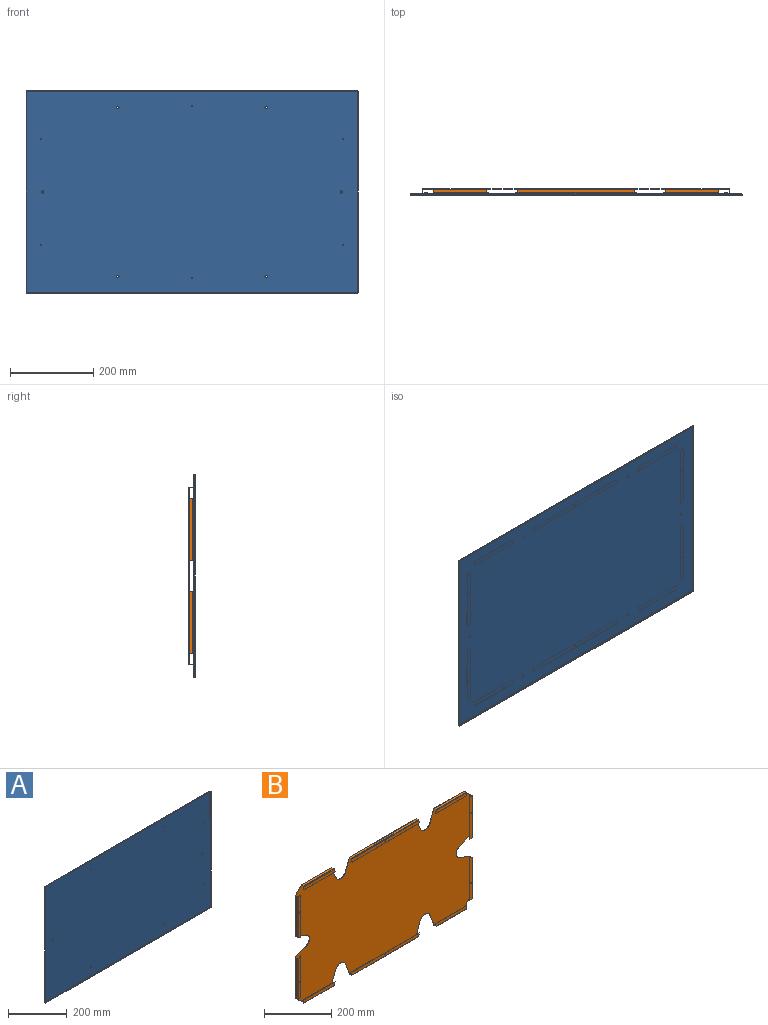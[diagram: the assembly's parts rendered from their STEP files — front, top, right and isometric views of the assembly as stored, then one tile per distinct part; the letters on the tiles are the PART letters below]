
ASSEMBLY  parts=2 mates=1
PART A: 50 faces, bbox 796.6x4x485.5 mm
  f0: plane 793.1x0.86mm, normal (0,-1,0), area 684.9mm2, adj f1,f2,f3,f4
  f1: plane 2.31x0.86mm, normal (1,0,0), area 2mm2, adj f0,f3,f4,f47
  f2: plane 2.31x0.86mm, normal (-1,0,0), area 2mm2, adj f0,f3,f4,f46
  f3: plane 793.1x2.31mm, normal (0,0,1), area 1833.2mm2, adj f0,f1,f2,f48
  f4: plane 793.1x2.31mm, normal (0,0,-1), area 1833.2mm2, adj f0,f1,f2,f49
  f5: cylinder r=1.63mm len=3.26mm, axis (0,-1,0), area 8.9mm2, adj f17,f18
  f6: cylinder r=1.63mm len=3.26mm, axis (0,-1,0), area 8.9mm2, adj f17,f18
  f7: cylinder r=1.63mm len=3.26mm, axis (0,-1,0), area 8.9mm2, adj f17,f18
  f8: cylinder r=1.63mm len=3.26mm, axis (0,-1,0), area 8.9mm2, adj f17,f18
  f9: cylinder r=1.63mm len=3.26mm, axis (0,-1,0), area 8.9mm2, adj f17,f18
  f10: cylinder r=1.63mm len=3.26mm, axis (0,-1,0), area 8.9mm2, adj f17,f18
  f11: cylinder r=2.77mm len=5.54mm, axis (0,-1,0), area 15mm2, adj f17,f18
  f12: cylinder r=2.77mm len=5.54mm, axis (0,-1,0), area 15mm2, adj f17,f18
  f13: cylinder r=2.77mm len=5.54mm, axis (0,-1,0), area 15mm2, adj f17,f18
  f14: cylinder r=2.77mm len=5.54mm, axis (0,-1,0), area 15mm2, adj f17,f18
  f15: cylinder r=2.77mm len=5.54mm, axis (0,-1,0), area 15mm2, adj f17,f18
  f16: cylinder r=2.77mm len=5.54mm, axis (0,-1,0), area 15mm2, adj f17,f18
  f17: plane 793.1x482.04mm, normal (0,1,0), area 382113.3mm2, adj f5,f6,f7,f8,f9,f10,f11,f12
  f18: plane 793.1x482.04mm, normal (0,-1,0), area 382113.3mm2, adj f5,f6,f7,f8,f9,f10,f11,f12
  f19: plane 793.1x0.86mm, normal (0,-1,0), area 684.9mm2, adj f20,f21,f22,f23
  f20: plane 2.31x0.86mm, normal (-1,0,0), area 2mm2, adj f19,f22,f23,f24
  f21: plane 2.31x0.86mm, normal (1,0,0), area 2mm2, adj f19,f22,f23,f25
  f22: plane 793.1x2.31mm, normal (0,0,-1), area 1833.2mm2, adj f19,f20,f21,f26
  f23: plane 793.1x2.31mm, normal (0,0,1), area 1833.2mm2, adj f19,f20,f21,f27
  f24: plane 1.73x1.73mm, normal (-1,0,0), area 1.8mm2, adj f20,f26,f27,f42
  f25: plane 1.73x1.73mm, normal (1,0,0), area 1.8mm2, adj f21,f26,f27,f33
  f26: cylinder r=1.73mm len=793.1mm, axis (-1,0,0), area 2151.7mm2, adj f17,f22,f24,f25
  f27: cylinder r=0.86mm len=793.1mm, axis (-1,0,0), area 1075.9mm2, adj f18,f23,f24,f25
  f28: plane 482.04x0.86mm, normal (0,-1,0), area 416.3mm2, adj f29,f30,f31,f32
  f29: plane 2.31x0.86mm, normal (0,0,-1), area 2mm2, adj f28,f31,f32,f33
  f30: plane 2.31x0.86mm, normal (0,0,1), area 2mm2, adj f28,f31,f32,f34
  f31: plane 482.04x2.31mm, normal (1,0,0), area 1114.2mm2, adj f28,f29,f30,f35
  f32: plane 482.04x2.31mm, normal (-1,0,0), area 1114.2mm2, adj f28,f29,f30,f36
  f33: plane 1.73x1.73mm, normal (0,0,-1), area 1.8mm2, adj f25,f29,f35,f36
  f34: plane 1.73x1.73mm, normal (0,0,1), area 1.8mm2, adj f30,f35,f36,f47
  f35: cylinder r=1.73mm len=482.04mm, axis (0,0,-1), area 1307.8mm2, adj f17,f31,f33,f34
  f36: cylinder r=0.86mm len=482.04mm, axis (0,0,-1), area 653.9mm2, adj f18,f32,f33,f34
  f37: plane 482.04x0.86mm, normal (0,-1,0), area 416.3mm2, adj f38,f39,f40,f41
  f38: plane 2.31x0.86mm, normal (0,0,1), area 2mm2, adj f37,f40,f41,f43
  f39: plane 2.31x0.86mm, normal (0,0,-1), area 2mm2, adj f37,f40,f41,f42
  f40: plane 482.04x2.31mm, normal (-1,0,0), area 1114.2mm2, adj f37,f38,f39,f44
  f41: plane 482.04x2.31mm, normal (1,0,0), area 1114.2mm2, adj f37,f38,f39,f45
  f42: plane 1.73x1.73mm, normal (0,0,-1), area 1.8mm2, adj f24,f39,f44,f45
  f43: plane 1.73x1.73mm, normal (0,0,1), area 1.8mm2, adj f38,f44,f45,f46
  f44: cylinder r=1.73mm len=482.04mm, axis (0,0,-1), area 1307.8mm2, adj f17,f40,f42,f43
  f45: cylinder r=0.86mm len=482.04mm, axis (0,0,-1), area 653.9mm2, adj f18,f41,f42,f43
  f46: plane 1.73x1.73mm, normal (-1,0,0), area 1.8mm2, adj f2,f43,f48,f49
  f47: plane 1.73x1.73mm, normal (1,0,0), area 1.8mm2, adj f1,f34,f48,f49
  f48: cylinder r=1.73mm len=793.1mm, axis (-1,0,0), area 2151.7mm2, adj f3,f17,f46,f47
  f49: cylinder r=0.86mm len=793.1mm, axis (-1,0,0), area 1075.9mm2, adj f4,f18,f46,f47
PART B: 200 faces, bbox 737.7x11.1x426.6 mm
  f0: plane 43.46x16.69mm, normal (-0.36,0,0.93), area 40.2mm2, adj f1,f22,f23,f143
  f1: cylinder r=22.23mm len=41.5mm, axis (0,-1,0), area 46.2mm2, adj f0,f2,f22,f23
  f2: plane 43.46x16.69mm, normal (-0.36,0,-0.93), area 40.2mm2, adj f1,f22,f23,f196
  f3: plane 23.67x23.67mm, normal (-0.71,0,0.71), area 28.9mm2, adj f22,f23,f111,f197
  f4: plane 43.46x16.69mm, normal (0.93,0,0.36), area 40.2mm2, adj f5,f22,f23,f112
  f5: cylinder r=22.23mm len=41.5mm, axis (0,-1,0), area 46.2mm2, adj f4,f6,f22,f23
  f6: plane 43.46x16.69mm, normal (-0.93,0,0.36), area 40.2mm2, adj f5,f22,f23,f107
  f7: plane 43.46x16.69mm, normal (0.93,0,0.36), area 40.2mm2, adj f8,f22,f23,f108
  f8: cylinder r=22.23mm len=41.5mm, axis (0,-1,0), area 46.2mm2, adj f7,f9,f22,f23
  f9: plane 43.46x16.69mm, normal (-0.93,0,0.36), area 40.2mm2, adj f8,f22,f23,f89
  f10: plane 23.67x23.67mm, normal (0.71,0,0.71), area 28.9mm2, adj f22,f23,f90,f179
  f11: plane 43.46x16.69mm, normal (0.36,0,-0.93), area 40.2mm2, adj f12,f22,f23,f178
  f12: cylinder r=22.23mm len=41.5mm, axis (0,-1,0), area 46.2mm2, adj f11,f13,f22,f23
  f13: plane 43.46x16.69mm, normal (0.36,0,0.93), area 40.2mm2, adj f12,f22,f23,f161
  f14: plane 23.67x23.67mm, normal (0.71,0,-0.71), area 28.9mm2, adj f22,f23,f73,f160
  f15: plane 43.46x16.69mm, normal (-0.93,0,-0.36), area 40.2mm2, adj f16,f22,f23,f72
  f16: cylinder r=22.23mm len=41.5mm, axis (0,-1,0), area 46.2mm2, adj f15,f17,f22,f23
  f17: plane 43.46x16.69mm, normal (0.93,0,-0.36), area 40.2mm2, adj f16,f22,f23,f56
  f18: plane 43.46x16.69mm, normal (-0.93,0,-0.36), area 40.2mm2, adj f19,f22,f23,f55
  f19: cylinder r=22.23mm len=41.5mm, axis (0,-1,0), area 46.2mm2, adj f18,f20,f22,f23
  f20: plane 43.46x16.69mm, normal (0.93,0,-0.36), area 40.2mm2, adj f19,f22,f23,f38
  f21: plane 23.67x23.67mm, normal (-0.71,0,-0.71), area 28.9mm2, adj f22,f23,f37,f142
  f22: plane 734.23x423.16mm, normal (0,1,0), area 291828.6mm2, adj f0,f1,f2,f3,f4,f5,f6,f7
  f23: plane 734.23x423.16mm, normal (0,-1,0), area 291828.6mm2, adj f0,f1,f2,f3,f4,f5,f6,f7
  f24: plane 10.97x4.21mm, normal (0.93,0,-0.36), area 10.2mm2, adj f25,f27,f28,f30
  f25: plane 131.55x0.86mm, normal (0,0,1), area 113.6mm2, adj f24,f26,f27,f28
  f26: plane 10.97x0.86mm, normal (-1,0,0), area 9.5mm2, adj f25,f27,f28,f29
  f27: plane 131.55x10.97mm, normal (0,-1,0), area 1420.4mm2, adj f24,f25,f26,f31
  f28: plane 131.55x10.97mm, normal (0,1,0), area 1420.4mm2, adj f24,f25,f26,f32
  f29: plane 1.73x1.73mm, normal (-1,0,0), area 1.8mm2, adj f26,f31,f32,f33
  f30: bspline ~1.73x1.73mm, area 1.8mm2, adj f24,f31,f32,f34
  f31: cylinder r=1.73mm len=127.34mm, axis (-1,0,0), area 345.5mm2, adj f27,f29,f30,f35
  f32: cylinder r=0.86mm len=127.34mm, axis (-1,0,0), area 172.7mm2, adj f28,f29,f30,f36
  f33: plane 7.66x0.86mm, normal (-1,0,0), area 6.6mm2, adj f29,f35,f36,f37
  f34: plane 7.66x0.86mm, normal (1,0,0), area 6.6mm2, adj f30,f35,f36,f38
  f35: plane 127.32x7.66mm, normal (0,0,-1), area 975mm2, adj f31,f33,f34,f39
  f36: plane 127.32x7.66mm, normal (0,0,1), area 975mm2, adj f32,f33,f34,f40
  f37: bspline ~1.73x1.73mm, area 2mm2, adj f21,f33,f39,f40
  f38: bspline ~1.73x1.73mm, area 1.8mm2, adj f20,f34,f39,f40
  f39: cylinder r=1.73mm len=128.2mm, axis (-1,0,0), area 346.1mm2, adj f22,f35,f37,f38
  f40: cylinder r=0.86mm len=128.2mm, axis (-1,0,0), area 173mm2, adj f23,f36,f37,f38
  f41: plane 10.97x4.21mm, normal (0.93,0,-0.36), area 10.2mm2, adj f42,f45,f46,f48
  f42: plane 289.15x0.86mm, normal (0,0,1), area 249.7mm2, adj f41,f43,f45,f46
  f43: plane 10.97x4.21mm, normal (-0.93,0,-0.36), area 10.2mm2, adj f42,f45,f46,f47
  f44: cylinder r=1.63mm len=3.26mm, axis (0,-1,0), area 8.9mm2, adj f45,f46
  f45: plane 289.15x10.97mm, normal (0,-1,0), area 3118.2mm2, adj f41,f42,f43,f44,f49
  f46: plane 289.15x10.97mm, normal (0,1,0), area 3118.2mm2, adj f41,f42,f43,f44,f50
  f47: bspline ~1.73x1.73mm, area 1.8mm2, adj f43,f49,f50,f51
  f48: bspline ~1.73x1.73mm, area 1.8mm2, adj f41,f49,f50,f52
  f49: cylinder r=1.73mm len=280.73mm, axis (-1,0,0), area 761.6mm2, adj f45,f47,f48,f53
  f50: cylinder r=0.86mm len=280.73mm, axis (-1,0,0), area 380.8mm2, adj f46,f47,f48,f54
  f51: plane 7.66x0.86mm, normal (-1,0,0), area 6.6mm2, adj f47,f53,f54,f55
  f52: plane 7.66x0.86mm, normal (1,0,0), area 6.6mm2, adj f48,f53,f54,f56
  f53: plane 280.69x7.66mm, normal (0,0,-1), area 2149.6mm2, adj f49,f51,f52,f57
  f54: plane 280.69x7.66mm, normal (0,0,1), area 2149.6mm2, adj f50,f51,f52,f58
  f55: bspline ~1.73x1.73mm, area 1.8mm2, adj f18,f51,f57,f58
  f56: bspline ~1.73x1.73mm, area 1.8mm2, adj f17,f52,f57,f58
  f57: cylinder r=1.73mm len=280.73mm, axis (-1,0,0), area 761.6mm2, adj f22,f53,f55,f56
  f58: cylinder r=0.86mm len=280.73mm, axis (-1,0,0), area 380.8mm2, adj f23,f54,f55,f56
  f59: plane 10.97x0.86mm, normal (1,0,0), area 9.5mm2, adj f60,f62,f63,f65
  f60: plane 131.55x0.86mm, normal (0,0,1), area 113.6mm2, adj f59,f61,f62,f63
  f61: plane 10.97x4.21mm, normal (-0.93,0,-0.36), area 10.2mm2, adj f60,f62,f63,f64
  f62: plane 131.55x10.97mm, normal (0,-1,0), area 1420.4mm2, adj f59,f60,f61,f66
  f63: plane 131.55x10.97mm, normal (0,1,0), area 1420.4mm2, adj f59,f60,f61,f67
  f64: bspline ~1.73x1.73mm, area 1.8mm2, adj f61,f66,f67,f69
  f65: plane 1.73x1.73mm, normal (1,0,0), area 1.8mm2, adj f59,f66,f67,f68
  f66: cylinder r=1.73mm len=127.34mm, axis (-1,0,0), area 345.5mm2, adj f62,f64,f65,f70
  f67: cylinder r=0.86mm len=127.34mm, axis (-1,0,0), area 172.7mm2, adj f63,f64,f65,f71
  f68: plane 7.66x0.86mm, normal (1,0,0), area 6.6mm2, adj f65,f70,f71,f73
  f69: plane 7.66x0.86mm, normal (-1,0,0), area 6.6mm2, adj f64,f70,f71,f72
  f70: plane 127.32x7.66mm, normal (0,0,-1), area 975mm2, adj f66,f68,f69,f74
  f71: plane 127.32x7.66mm, normal (0,0,1), area 975mm2, adj f67,f68,f69,f75
  f72: bspline ~1.73x1.73mm, area 1.8mm2, adj f15,f69,f74,f75
  f73: bspline ~1.73x1.73mm, area 2mm2, adj f14,f68,f74,f75
  f74: cylinder r=1.73mm len=128.2mm, axis (-1,0,0), area 346.1mm2, adj f22,f70,f72,f73
  f75: cylinder r=0.86mm len=128.2mm, axis (-1,0,0), area 173mm2, adj f23,f71,f72,f73
  f76: plane 7.66x0.86mm, normal (1,0,0), area 6.6mm2, adj f78,f79,f81,f90
  f77: plane 7.66x0.86mm, normal (-1,0,0), area 6.6mm2, adj f78,f79,f80,f89
  f78: plane 127.32x7.66mm, normal (0,0,1), area 975mm2, adj f76,f77,f82,f91
  f79: plane 127.32x7.66mm, normal (0,0,-1), area 975mm2, adj f76,f77,f83,f92
  f80: bspline ~1.73x1.73mm, area 1.8mm2, adj f77,f82,f83,f84
  f81: plane 1.73x1.73mm, normal (1,0,0), area 1.8mm2, adj f76,f82,f83,f86
  f82: cylinder r=1.73mm len=127.34mm, axis (-1,0,0), area 345.5mm2, adj f78,f80,f81,f87
  f83: cylinder r=0.86mm len=127.34mm, axis (-1,0,0), area 172.7mm2, adj f79,f80,f81,f88
  f84: plane 10.97x4.21mm, normal (-0.93,0,0.36), area 10.2mm2, adj f80,f85,f87,f88
  f85: plane 131.55x0.86mm, normal (0,0,-1), area 113.6mm2, adj f84,f86,f87,f88
  f86: plane 10.97x0.86mm, normal (1,0,0), area 9.5mm2, adj f81,f85,f87,f88
  f87: plane 131.55x10.97mm, normal (0,-1,0), area 1420.4mm2, adj f82,f84,f85,f86
  f88: plane 131.55x10.97mm, normal (0,1,0), area 1420.4mm2, adj f83,f84,f85,f86
  f89: bspline ~1.73x1.73mm, area 1.8mm2, adj f9,f77,f91,f92
  f90: bspline ~1.73x1.73mm, area 2mm2, adj f10,f76,f91,f92
  f91: cylinder r=1.73mm len=128.2mm, axis (-1,0,0), area 346.1mm2, adj f22,f78,f89,f90
  f92: cylinder r=0.86mm len=128.2mm, axis (-1,0,0), area 173mm2, adj f23,f79,f89,f90
  f93: plane 10.97x4.21mm, normal (-0.93,0,0.36), area 10.2mm2, adj f94,f97,f98,f99
  f94: plane 289.15x0.86mm, normal (0,0,-1), area 249.7mm2, adj f93,f95,f97,f98
  f95: plane 10.97x4.21mm, normal (0.93,0,0.36), area 10.2mm2, adj f94,f97,f98,f100
  f96: cylinder r=1.63mm len=3.26mm, axis (0,-1,0), area 8.9mm2, adj f97,f98
  f97: plane 289.15x10.97mm, normal (0,-1,0), area 3118.2mm2, adj f93,f94,f95,f96,f101
  f98: plane 289.15x10.97mm, normal (0,1,0), area 3118.2mm2, adj f93,f94,f95,f96,f102
  f99: bspline ~1.73x1.73mm, area 1.8mm2, adj f93,f101,f102,f103
  f100: bspline ~1.73x1.73mm, area 1.8mm2, adj f95,f101,f102,f104
  f101: cylinder r=1.73mm len=280.73mm, axis (-1,0,0), area 761.6mm2, adj f97,f99,f100,f105
  f102: cylinder r=0.86mm len=280.73mm, axis (-1,0,0), area 380.8mm2, adj f98,f99,f100,f106
  f103: plane 7.66x0.86mm, normal (-1,0,0), area 6.6mm2, adj f99,f105,f106,f107
  f104: plane 7.66x0.86mm, normal (1,0,0), area 6.6mm2, adj f100,f105,f106,f108
  f105: plane 280.69x7.66mm, normal (0,0,1), area 2149.6mm2, adj f101,f103,f104,f109
  f106: plane 280.69x7.66mm, normal (0,0,-1), area 2149.6mm2, adj f102,f103,f104,f110
  f107: bspline ~1.73x1.73mm, area 1.8mm2, adj f6,f103,f109,f110
  f108: bspline ~1.73x1.73mm, area 1.8mm2, adj f7,f104,f109,f110
  f109: cylinder r=1.73mm len=280.73mm, axis (-1,0,0), area 761.6mm2, adj f22,f105,f107,f108
  f110: cylinder r=0.86mm len=280.73mm, axis (-1,0,0), area 380.8mm2, adj f23,f106,f107,f108
  f111: bspline ~1.73x1.73mm, area 2mm2, adj f3,f113,f114,f115
  f112: bspline ~1.73x1.73mm, area 1.8mm2, adj f4,f113,f114,f116
  f113: cylinder r=1.73mm len=128.2mm, axis (-1,0,0), area 346.1mm2, adj f22,f111,f112,f117
  f114: cylinder r=0.86mm len=128.2mm, axis (-1,0,0), area 173mm2, adj f23,f111,f112,f118
  f115: plane 7.66x0.86mm, normal (-1,0,0), area 6.6mm2, adj f111,f117,f118,f124
  f116: plane 7.66x0.86mm, normal (1,0,0), area 6.6mm2, adj f112,f117,f118,f125
  f117: plane 127.32x7.66mm, normal (0,0,1), area 975mm2, adj f113,f115,f116,f126
  f118: plane 127.32x7.66mm, normal (0,0,-1), area 975mm2, adj f114,f115,f116,f127
  f119: plane 10.97x0.86mm, normal (-1,0,0), area 9.5mm2, adj f120,f122,f123,f124
  f120: plane 131.55x0.86mm, normal (0,0,-1), area 113.6mm2, adj f119,f121,f122,f123
  f121: plane 10.97x4.21mm, normal (0.93,0,0.36), area 10.2mm2, adj f120,f122,f123,f125
  f122: plane 131.55x10.97mm, normal (0,-1,0), area 1420.4mm2, adj f119,f120,f121,f126
  f123: plane 131.55x10.97mm, normal (0,1,0), area 1420.4mm2, adj f119,f120,f121,f127
  f124: plane 1.73x1.73mm, normal (-1,0,0), area 1.8mm2, adj f115,f119,f126,f127
  f125: bspline ~1.73x1.73mm, area 1.8mm2, adj f116,f121,f126,f127
  f126: cylinder r=1.73mm len=127.34mm, axis (-1,0,0), area 345.5mm2, adj f117,f122,f124,f125
  f127: cylinder r=0.86mm len=127.34mm, axis (-1,0,0), area 172.7mm2, adj f118,f123,f124,f125
  f128: plane 10.97x0.86mm, normal (0,0,-1), area 9.5mm2, adj f129,f132,f133,f134
  f129: plane 153.82x0.86mm, normal (1,0,0), area 132.8mm2, adj f128,f130,f132,f133
  f130: plane 10.97x4.21mm, normal (-0.36,0,0.93), area 10.2mm2, adj f129,f132,f133,f135
  f131: cylinder r=1.63mm len=3.26mm, axis (0,-1,0), area 8.9mm2, adj f132,f133
  f132: plane 153.82x10.97mm, normal (0,-1,0), area 1656.4mm2, adj f128,f129,f130,f131,f136
  f133: plane 153.82x10.97mm, normal (0,1,0), area 1656.4mm2, adj f128,f129,f130,f131,f137
  f134: plane 1.73x1.73mm, normal (0,0,-1), area 1.8mm2, adj f128,f136,f137,f138
  f135: bspline ~1.73x1.73mm, area 1.8mm2, adj f130,f136,f137,f139
  f136: cylinder r=1.73mm len=149.61mm, axis (0,0,-1), area 405.9mm2, adj f132,f134,f135,f140
  f137: cylinder r=0.86mm len=149.61mm, axis (0,0,-1), area 202.9mm2, adj f133,f134,f135,f141
  f138: plane 7.66x0.86mm, normal (0,0,-1), area 6.6mm2, adj f134,f140,f141,f142
  f139: plane 7.66x0.86mm, normal (0,0,1), area 6.6mm2, adj f135,f140,f141,f143
  f140: plane 149.59x7.66mm, normal (-1,0,0), area 1145.6mm2, adj f136,f138,f139,f144
  f141: plane 149.59x7.66mm, normal (1,0,0), area 1145.6mm2, adj f137,f138,f139,f145
  f142: bspline ~1.73x1.73mm, area 2mm2, adj f21,f138,f144,f145
  f143: bspline ~1.73x1.73mm, area 1.8mm2, adj f0,f139,f144,f145
  f144: cylinder r=1.73mm len=150.47mm, axis (0,0,-1), area 406.5mm2, adj f22,f140,f142,f143
  f145: cylinder r=0.86mm len=150.47mm, axis (0,0,-1), area 203.2mm2, adj f23,f141,f142,f143
  f146: plane 153.82x0.86mm, normal (-1,0,0), area 132.8mm2, adj f147,f149,f150,f151
  f147: plane 10.97x0.86mm, normal (0,0,-1), area 9.5mm2, adj f146,f150,f151,f152
  f148: cylinder r=1.63mm len=3.26mm, axis (0,-1,0), area 8.9mm2, adj f150,f151
  f149: plane 10.97x4.21mm, normal (0.36,0,0.93), area 10.2mm2, adj f146,f150,f151,f153
  f150: plane 153.82x10.97mm, normal (0,-1,0), area 1656.4mm2, adj f146,f147,f148,f149,f154
  f151: plane 153.82x10.97mm, normal (0,1,0), area 1656.4mm2, adj f146,f147,f148,f149,f155
  f152: plane 1.73x1.73mm, normal (0,0,-1), area 1.8mm2, adj f147,f154,f155,f156
  f153: bspline ~1.73x1.73mm, area 1.8mm2, adj f149,f154,f155,f157
  f154: cylinder r=1.73mm len=149.61mm, axis (0,0,-1), area 405.9mm2, adj f150,f152,f153,f158
  f155: cylinder r=0.86mm len=149.61mm, axis (0,0,-1), area 202.9mm2, adj f151,f152,f153,f159
  f156: plane 7.66x0.86mm, normal (0,0,-1), area 6.6mm2, adj f152,f158,f159,f160
  f157: plane 7.66x0.86mm, normal (0,0,1), area 6.6mm2, adj f153,f158,f159,f161
  f158: plane 149.59x7.66mm, normal (1,0,0), area 1145.6mm2, adj f154,f156,f157,f162
  f159: plane 149.59x7.66mm, normal (-1,0,0), area 1145.6mm2, adj f155,f156,f157,f163
  f160: bspline ~1.73x1.73mm, area 2mm2, adj f14,f156,f162,f163
  f161: bspline ~1.73x1.73mm, area 1.8mm2, adj f13,f157,f162,f163
  f162: cylinder r=1.73mm len=150.47mm, axis (0,0,-1), area 406.5mm2, adj f22,f158,f160,f161
  f163: cylinder r=0.86mm len=150.47mm, axis (0,0,-1), area 203.2mm2, adj f23,f159,f160,f161
  f164: plane 10.97x0.86mm, normal (0,0,1), area 9.5mm2, adj f165,f168,f169,f171
  f165: plane 153.82x0.86mm, normal (-1,0,0), area 132.8mm2, adj f164,f166,f168,f169
  f166: plane 10.97x4.21mm, normal (0.36,0,-0.93), area 10.2mm2, adj f165,f168,f169,f170
  f167: cylinder r=1.63mm len=3.26mm, axis (0,-1,0), area 8.9mm2, adj f168,f169
  f168: plane 153.82x10.97mm, normal (0,-1,0), area 1656.4mm2, adj f164,f165,f166,f167,f172
  f169: plane 153.82x10.97mm, normal (0,1,0), area 1656.4mm2, adj f164,f165,f166,f167,f173
  f170: bspline ~1.73x1.73mm, area 1.8mm2, adj f166,f172,f173,f175
  f171: plane 1.73x1.73mm, normal (0,0,1), area 1.8mm2, adj f164,f172,f173,f174
  f172: cylinder r=1.73mm len=149.61mm, axis (0,0,-1), area 405.9mm2, adj f168,f170,f171,f176
  f173: cylinder r=0.86mm len=149.61mm, axis (0,0,-1), area 202.9mm2, adj f169,f170,f171,f177
  f174: plane 7.66x0.86mm, normal (0,0,1), area 6.6mm2, adj f171,f176,f177,f179
  f175: plane 7.66x0.86mm, normal (0,0,-1), area 6.6mm2, adj f170,f176,f177,f178
  f176: plane 149.59x7.66mm, normal (1,0,0), area 1145.6mm2, adj f172,f174,f175,f180
  f177: plane 149.59x7.66mm, normal (-1,0,0), area 1145.6mm2, adj f173,f174,f175,f181
  f178: bspline ~1.73x1.73mm, area 1.8mm2, adj f11,f175,f180,f181
  f179: bspline ~1.73x1.73mm, area 2mm2, adj f10,f174,f180,f181
  f180: cylinder r=1.73mm len=150.47mm, axis (0,0,-1), area 406.5mm2, adj f22,f176,f178,f179
  f181: cylinder r=0.86mm len=150.47mm, axis (0,0,-1), area 203.2mm2, adj f23,f177,f178,f179
  f182: plane 153.82x0.86mm, normal (1,0,0), area 132.8mm2, adj f183,f185,f186,f187
  f183: plane 10.97x0.86mm, normal (0,0,1), area 9.5mm2, adj f182,f186,f187,f189
  f184: cylinder r=1.63mm len=3.26mm, axis (0,-1,0), area 8.9mm2, adj f186,f187
  f185: plane 10.97x4.21mm, normal (-0.36,0,-0.93), area 10.2mm2, adj f182,f186,f187,f188
  f186: plane 153.82x10.97mm, normal (0,-1,0), area 1656.4mm2, adj f182,f183,f184,f185,f190
  f187: plane 153.82x10.97mm, normal (0,1,0), area 1656.4mm2, adj f182,f183,f184,f185,f191
  f188: bspline ~1.73x1.73mm, area 1.8mm2, adj f185,f190,f191,f193
  f189: plane 1.73x1.73mm, normal (0,0,1), area 1.8mm2, adj f183,f190,f191,f192
  f190: cylinder r=1.73mm len=149.61mm, axis (0,0,-1), area 405.9mm2, adj f186,f188,f189,f194
  f191: cylinder r=0.86mm len=149.61mm, axis (0,0,-1), area 202.9mm2, adj f187,f188,f189,f195
  f192: plane 7.66x0.86mm, normal (0,0,1), area 6.6mm2, adj f189,f194,f195,f197
  f193: plane 7.66x0.86mm, normal (0,0,-1), area 6.6mm2, adj f188,f194,f195,f196
  f194: plane 149.59x7.66mm, normal (-1,0,0), area 1145.6mm2, adj f190,f192,f193,f198
  f195: plane 149.59x7.66mm, normal (1,0,0), area 1145.6mm2, adj f191,f192,f193,f199
  f196: bspline ~1.73x1.73mm, area 1.8mm2, adj f2,f193,f198,f199
  f197: bspline ~1.73x1.73mm, area 2mm2, adj f3,f192,f198,f199
  f198: cylinder r=1.73mm len=150.47mm, axis (0,0,-1), area 406.5mm2, adj f22,f194,f196,f197
  f199: cylinder r=0.86mm len=150.47mm, axis (0,0,-1), area 203.2mm2, adj f23,f195,f196,f197
PLACE A at identity fixed
PLACE B t=(0,6.42,0.03)mm
MATE fastened B.f97 <-> A.f10  axis (0,-1,0) through (0,0.86,206.1)mm
